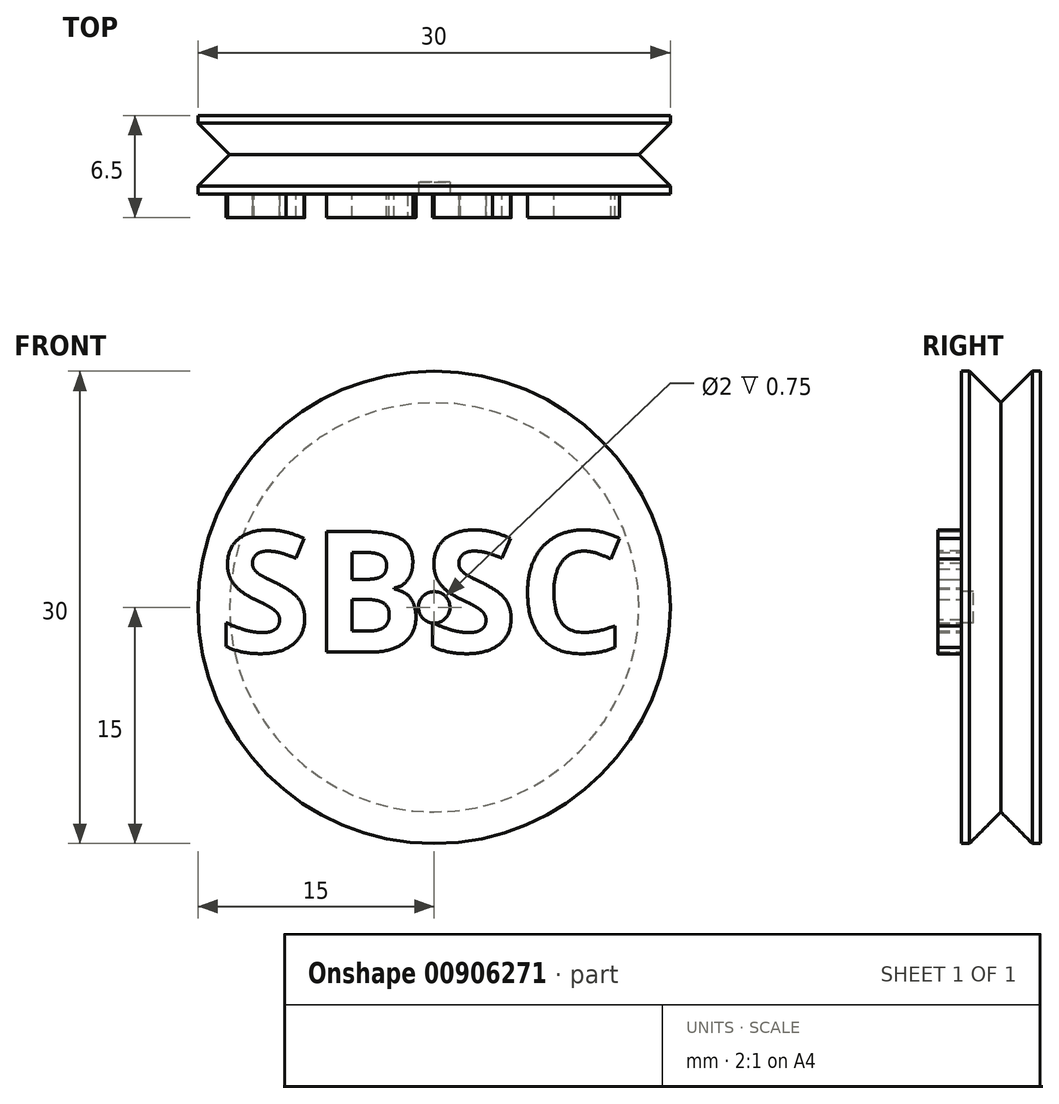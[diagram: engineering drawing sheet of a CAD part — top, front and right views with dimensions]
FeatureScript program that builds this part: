
annotation { "Feature Type Name" : "Feature", "Feature Type Description" : "" }
export const myFeature = defineFeature(function(context is Context, id is Id, definition is map)
    precondition{}
    {
        {
            var Q0;
            Q0=qCreatedBy(makeId("Front.planeOp"),FACE);
            var sketch = newSketch(context, id + "F0", { "sketchPlane" : qUnion([Q0])});
            skCircle(sketch, "E0", {"center": v(0, 0) * mm, "radius": 15 * mm});
            skSolve(sketch);
        }
        {
            var Q0;
            Q0=makeQuery(id+"F0.imprint","IMPRINT",FACE,{"disambiguationData":[TD([[makeQuery(id+"F0.imprint","IMPRINT",EDGE,{"derivedFrom":sQuery(id+"F0.wireOp",EDGE,"E0")}),1.0]])]});
            extrude(context, id + "F1", {"entities" : qUnion([Q0]), "depth" : 2.5 * mm, "offsetDistance" : 25 * mm});
        }
        {
            var Q0;
            Q0=makeQuery(id+"F1.opExtrude","CAP_EDGE",EDGE,{"disambiguationData":[OSD([sQuery(id+"F0.wireOp",EDGE,"E0")])],"isStart":false});
            chamfer(context, id + "F2", {"entities" : qUnion([Q0]), "width" : 2 * mm, "tangentPropagation" : true});
        }
        {
            var Q0;
            Q0=makeQuery(id+"F1.opExtrude","CAP_FACE",FACE,{"disambiguationData":[OSD([sQuery(id+"F0.wireOp",EDGE,"E0")])],"isStart":false});
            var sketch = newSketch(context, id + "F3", { "sketchPlane" : qUnion([Q0])});
            skCircle(sketch, "E1", {"center": v(0, 0) * mm, "radius": 15 * mm});
            skSolve(sketch);
        }
        {
            var Q0;
            Q0=makeQuery(id+"F3.imprint","IMPRINT",FACE,{"disambiguationData":[TD([[makeQuery(id+"F3.imprint","IMPRINT",EDGE,{"derivedFrom":sQuery(id+"F3.wireOp",EDGE,"E1")}),1.0]])]});
            var Q1;
            {var subQ0=sQuery(id+"F0.wireOp",EDGE,"E0");Q1=makeQuery(id+"F3.imprint","IMPRINT",FACE,{"disambiguationData":[TD([[makeQuery(id+"F3.imprint","IMPRINT",EDGE,{"derivedFrom":makeQuery(id+"F2.opChamfer","BLEND_EDGE",EDGE,{"blendedFrom":[makeQuery(id+"F1.opExtrude","CAP_EDGE",EDGE,{"disambiguationData":[OSD([subQ0])],"isStart":false}),makeQuery(id+"F1.opExtrude","CAP_FACE",FACE,{"disambiguationData":[OSD([subQ0])],"isStart":false})],"blendedInto":[makeQuery(id+"F1.opExtrude","CAP_FACE",FACE,{"disambiguationData":[OSD([subQ0])],"isStart":false})]})}),1.0]])]});}
            extrude(context, id + "F4", {"entities" : qUnion([Q0, Q1]), "operationType" : NewBodyOperationType.ADD, "depth" : 2.5 * mm, "offsetDistance" : 25 * mm});
        }
        {
            var Q0;
            Q0=makeQuery(id+"F4.opExtrude","CAP_EDGE",EDGE,{"disambiguationData":[OSD([sQuery(id+"F3.wireOp",EDGE,"E1")])],"isStart":true});
            chamfer(context, id + "F5", {"entities" : qUnion([Q0]), "width" : 2 * mm, "tangentPropagation" : true});
        }
        {
            var Q0;
            Q0=makeQuery(id+"F4.opExtrude","CAP_FACE",FACE,{"disambiguationData":[OSD([sQuery(id+"F3.wireOp",EDGE,"E1")])],"isStart":false});
            var sketch = newSketch(context, id + "F6", { "sketchPlane" : qUnion([Q0])});
            skCircle(sketch, "E2", {"center": v(0, 0) * mm, "radius": 1 * mm});
            skSolve(sketch);
        }
        {
            var Q0;
            Q0=makeQuery(id+"F6.imprint","IMPRINT",FACE,{"disambiguationData":[TD([[makeQuery(id+"F6.imprint","IMPRINT",EDGE,{"derivedFrom":sQuery(id+"F6.wireOp",EDGE,"E2")}),1.0]])]});
            extrude(context, id + "F7", {"entities" : qUnion([Q0]), "operationType" : NewBodyOperationType.REMOVE, "oppositeDirection" : true, "depth" : 0.75 * mm, "offsetDistance" : 25 * mm});
        }
        {
            var Q0;
            Q0=makeQuery(id+"F4.opExtrude","CAP_FACE",FACE,{"disambiguationData":[OSD([sQuery(id+"F3.wireOp",EDGE,"E1")])],"isStart":false});
            var sketch = newSketch(context, id + "F8", { "sketchPlane" : qUnion([Q0])});
            skText(sketch, "E3", { "text": "SBSC", "fontName": "OpenSans-Bold.ttf"});
            const initialGuessF8  = {"E3": [-0.01371, -0.00284, 1, 0, 0.00772]};
            skSetInitialGuess(sketch, initialGuessF8);
            skSolve(sketch);
        }
        {
            var Q0;
            Q0=qSketchRegion(id+"F8",true);
            extrude(context, id + "F9", {"entities" : qUnion([Q0]), "operationType" : NewBodyOperationType.ADD, "depth" : 1.5 * mm, "offsetDistance" : 25 * mm});
        }
    });
